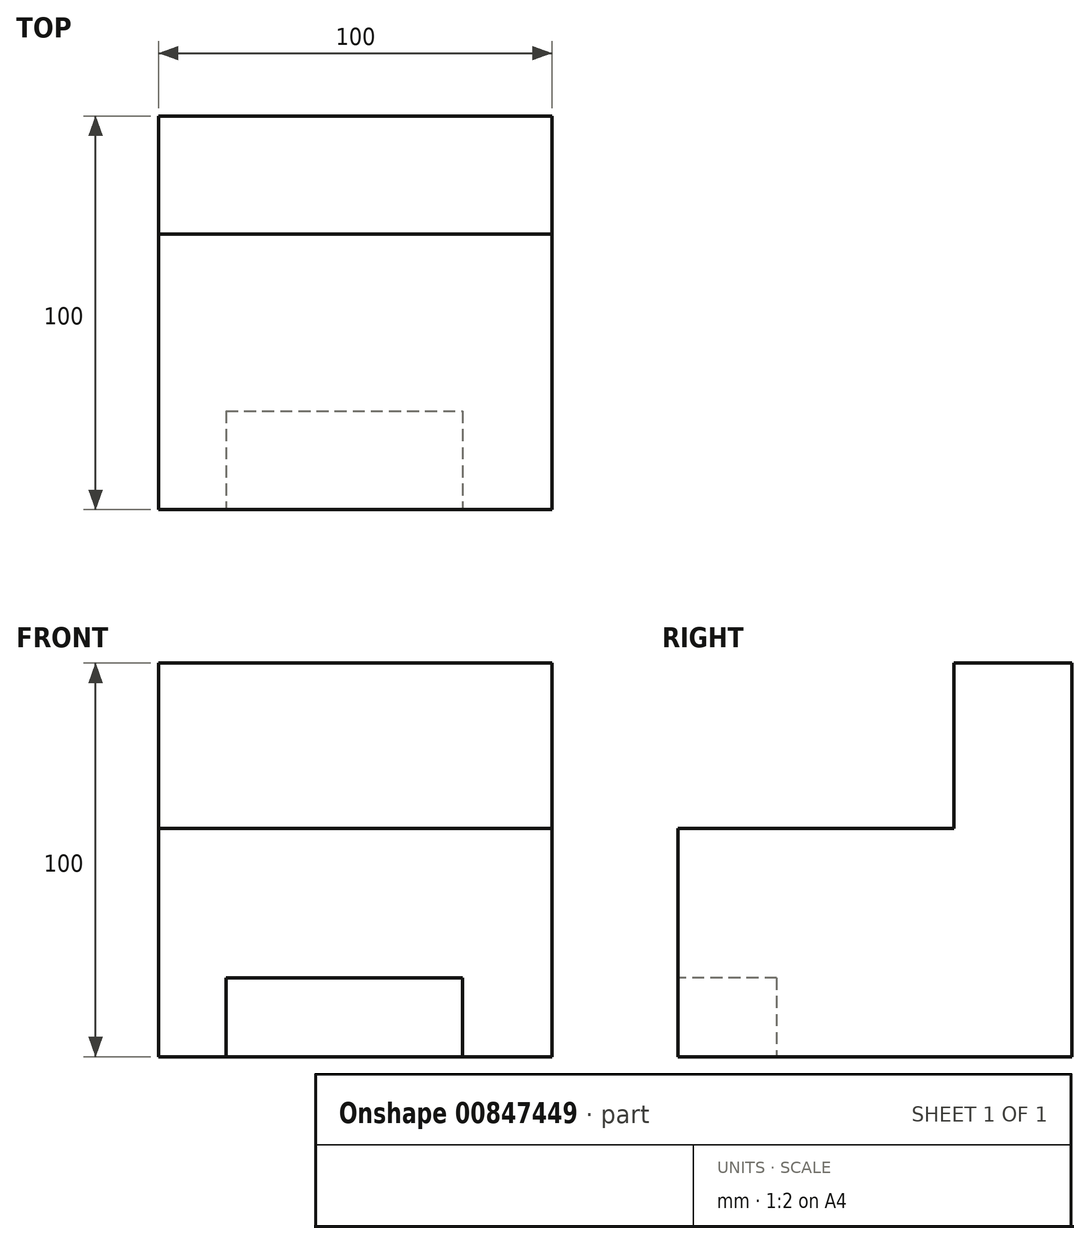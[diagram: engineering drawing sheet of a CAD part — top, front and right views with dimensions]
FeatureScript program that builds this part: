
annotation { "Feature Type Name" : "Feature", "Feature Type Description" : "" }
export const myFeature = defineFeature(function(context is Context, id is Id, definition is map)
    precondition{}
    {
        {
            var Q0;
            Q0=qCreatedBy(makeId("Top.planeOp"),FACE);
            var sketch = newSketch(context, id + "F0", { "sketchPlane" : qUnion([Q0])});
            skLineSegment(sketch, "E0.bottom", {"start": v(-50, 50) * mm, "end": v(50, 50) * mm});
            skLineSegment(sketch, "E0.top", {"start": v(-50, -50) * mm, "end": v(50, -50) * mm});
            skLineSegment(sketch, "E0.left", {"start": v(-50, 50) * mm, "end": v(-50, -50) * mm});
            skLineSegment(sketch, "E0.right", {"start": v(50, 50) * mm, "end": v(50, -50) * mm});
            skPoint(sketch, "E0.middle", {"position": v(0, 0) * mm});
            skSolve(sketch);
        }
        {
            var Q0;
            Q0=makeQuery(id+"F0.imprint","IMPRINT",FACE,{"disambiguationData":[TD([[makeQuery(id+"F0.imprint","IMPRINT",EDGE,{"derivedFrom":sQuery(id+"F0.wireOp",EDGE,"E0.bottom")}),-1.0]])]});
            extrude(context, id + "F1", {"entities" : qUnion([Q0]), "depth" : 100 * mm, "offsetDistance" : 25 * mm});
        }
        {
            var Q0;
            Q0=makeQuery(id+"F1.opExtrude","CAP_FACE",FACE,{"disambiguationData":[OSD([sQuery(id+"F0.wireOp",EDGE,"E0.bottom"),sQuery(id+"F0.wireOp",EDGE,"E0.top"),sQuery(id+"F0.wireOp",EDGE,"E0.left"),sQuery(id+"F0.wireOp",EDGE,"E0.right")])],"isStart":false});
            var sketch = newSketch(context, id + "F2", { "sketchPlane" : qUnion([Q0])});
            skLineSegment(sketch, "E1.bottom", {"start": v(-50, 20) * mm, "end": v(50, 20) * mm});
            skLineSegment(sketch, "E1.top", {"start": v(-50, -50) * mm, "end": v(50, -50) * mm});
            skLineSegment(sketch, "E1.left", {"start": v(-50, 20) * mm, "end": v(-50, -50) * mm});
            skLineSegment(sketch, "E1.right", {"start": v(50, 20) * mm, "end": v(50, -50) * mm});
            skSolve(sketch);
        }
        {
            var Q0;
            Q0=makeQuery(id+"F2.imprint","IMPRINT",FACE,{"disambiguationData":[TD([[makeQuery(id+"F2.imprint","IMPRINT",EDGE,{"derivedFrom":sQuery(id+"F2.wireOp",EDGE,"E1.bottom")}),-1.0]])]});
            extrude(context, id + "F3", {"entities" : qUnion([Q0]), "operationType" : NewBodyOperationType.REMOVE, "oppositeDirection" : true, "depth" : 42 * mm, "offsetDistance" : 25 * mm});
        }
        {
            var Q0;
            Q0=makeQuery(id+"F1.opExtrude","SWEPT_FACE",FACE,{"disambiguationData":[OSD([sQuery(id+"F0.wireOp",EDGE,"E0.top")])]});
            var sketch = newSketch(context, id + "F4", { "sketchPlane" : qUnion([Q0])});
            skLineSegment(sketch, "E2.bottom", {"start": v(-32.85, 20) * mm, "end": v(27.15, 20) * mm});
            skLineSegment(sketch, "E2.top", {"start": v(-32.85, 0) * mm, "end": v(27.15, 0) * mm});
            skLineSegment(sketch, "E2.left", {"start": v(-32.85, 20) * mm, "end": v(-32.85, 0) * mm});
            skLineSegment(sketch, "E2.right", {"start": v(27.15, 20) * mm, "end": v(27.15, 0) * mm});
            skSolve(sketch);
        }
        {
            var Q0;
            Q0=makeQuery(id+"F4.imprint","IMPRINT",FACE,{"disambiguationData":[TD([[makeQuery(id+"F4.imprint","IMPRINT",EDGE,{"derivedFrom":sQuery(id+"F4.wireOp",EDGE,"E2.bottom")}),-1.0]])]});
            extrude(context, id + "F5", {"entities" : qUnion([Q0]), "operationType" : NewBodyOperationType.REMOVE, "oppositeDirection" : true, "depth" : 25 * mm, "offsetDistance" : 25 * mm});
        }
    });
